# Revit family: Bernhardt_Design-Seating-Guest-Pedersen
name_source: partatom
category: Furniture
revit_build: Autodesk Revit 2016 (Build: 20150714_1515(x64)
units: mm (PartAtom-declared; Revit-internal decimal feet)

## family parameters
Always vertical = Yes
Cut with Voids When Loaded = No
Room Calculation Point = No
Shared = Yes

## types (6) — shared parameters
Manufacturer = Bernhardt Design
Model = Pedersen
URL = http://bernhardtdesign.com

## per-type parameters (varying)
| type | Base Metal | SKU | Wood Veneer |
| Pedersen - 1111C | Copper - Polished | Pedersen 1111C | Bernhardt - Oak default |
| Pedersen - 1111K | Chrome - Black | Pedersen 1111K | Bernhardt - Oak default |
| Pedersen - 1111P | Chrome - Polished | Pedersen 1111P | Bernhardt - Oak default |
| Pedersen - 1112C | Copper - Polished | Pedersen 1112C | Bernhardt - Walnut default |
| Pedersen - 1112K | Chrome - Black | Pedersen 1112K | Bernhardt - Walnut default |
| Pedersen - 1112P | Chrome - Polished | Pedersen 1112P | Bernhardt - Walnut default |

## geometry (parser evidence)
native form markers: Sweep x2
no freeform markers — native parametric forms only
